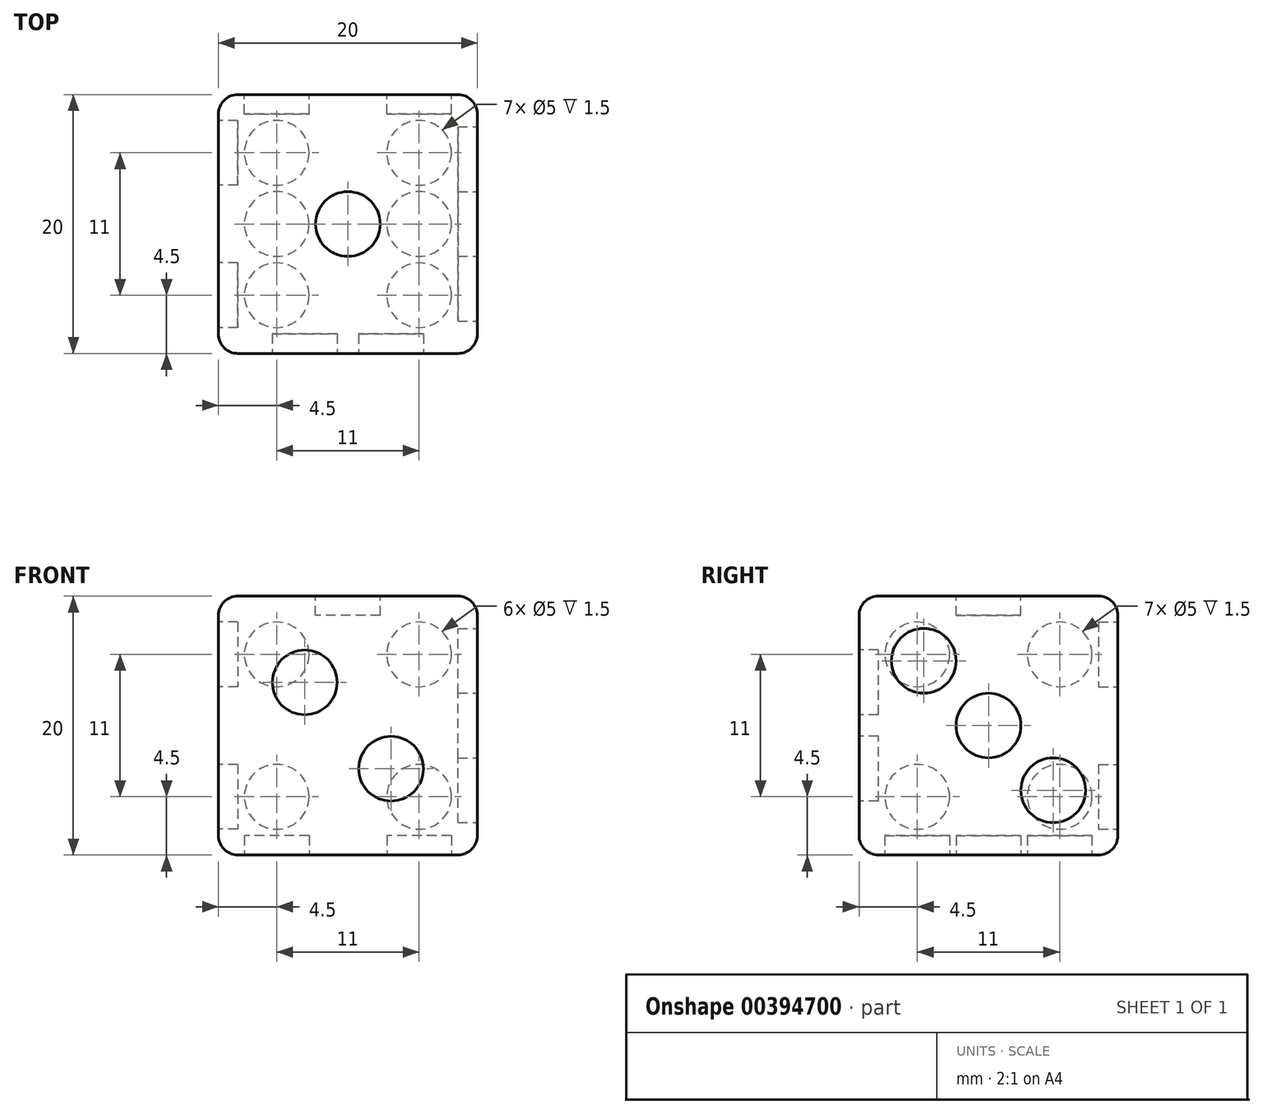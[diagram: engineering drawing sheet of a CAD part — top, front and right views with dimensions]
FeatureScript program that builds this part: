
annotation { "Feature Type Name" : "Feature", "Feature Type Description" : "" }
export const myFeature = defineFeature(function(context is Context, id is Id, definition is map)
    precondition{}
    {
        {
            assignVariable(context, id + "F0", {"name" : "Extrude", "anyValue" : -1.5});
        }
        {
            var Q0;
            Q0=qCreatedBy(makeId("Top.planeOp"),FACE);
            var sketch = newSketch(context, id + "F1", { "sketchPlane" : qUnion([Q0])});
            skLineSegment(sketch, "E0.bottom", {"start": v(10, 10) * mm, "end": v(-10, 10) * mm});
            skLineSegment(sketch, "E0.top", {"start": v(10, -10) * mm, "end": v(-10, -10) * mm});
            skLineSegment(sketch, "E0.left", {"start": v(10, 10) * mm, "end": v(10, -10) * mm});
            skLineSegment(sketch, "E0.right", {"start": v(-10, 10) * mm, "end": v(-10, -10) * mm});
            skPoint(sketch, "E0.middle", {"position": v(0, 0) * mm});
            skSolve(sketch);
        }
        {
            var Q0;
            Q0=makeQuery(id+"F1.imprint","IMPRINT",FACE,{"disambiguationData":[TD([[makeQuery(id+"F1.imprint","IMPRINT",EDGE,{"derivedFrom":sQuery(id+"F1.wireOp",EDGE,"E0.bottom")}),1.0]])]});
            extrude(context, id + "F2", {"entities" : qUnion([Q0]), "depth" : 20 * mm});
        }
        {
            var Q0;
            Q0=makeQuery(id+"F2.opExtrude","CAP_FACE",FACE,{"disambiguationData":[OSD([sQuery(id+"F1.wireOp",EDGE,"E0.bottom"),sQuery(id+"F1.wireOp",EDGE,"E0.top"),sQuery(id+"F1.wireOp",EDGE,"E0.left"),sQuery(id+"F1.wireOp",EDGE,"E0.right")])],"isStart":false});
            var sketch = newSketch(context, id + "F3", { "sketchPlane" : qUnion([Q0])});
            skCircle(sketch, "E1", {"center": v(0, 0) * mm, "radius": 2.5 * mm});
            skSolve(sketch);
        }
        {
            var Q0;
            Q0=makeQuery(id+"F1.imprint","IMPRINT",FACE,{"disambiguationData":[TD([[makeQuery(id+"F1.imprint","IMPRINT",EDGE,{"derivedFrom":sQuery(id+"F1.wireOp",EDGE,"E0.bottom")}),1.0]])]});
            var sketch = newSketch(context, id + "F4", { "sketchPlane" : qUnion([Q0])});
            skCircle(sketch, "E2", {"center": v(-5.5, -5.5) * mm, "radius": 2.5 * mm});
            skCircle(sketch, "E3", {"center": v(5.5, -5.5) * mm, "radius": 2.5 * mm});
            skCircle(sketch, "E4", {"center": v(5.5, 5.5) * mm, "radius": 2.5 * mm});
            skCircle(sketch, "E5", {"center": v(-5.5, 5.5) * mm, "radius": 2.5 * mm});
            skCircle(sketch, "E6", {"center": v(5.5, 0) * mm, "radius": 2.5 * mm});
            skCircle(sketch, "E7", {"center": v(-5.5, 0) * mm, "radius": 2.5 * mm});
            skLineSegment(sketch, "E8.0", {"start": v(10, -10) * mm, "end": v(-10, -10) * mm});
            skLineSegment(sketch, "E9.0", {"start": v(-10, 10) * mm, "end": v(-10, -10) * mm});
            skLineSegment(sketch, "E10.0", {"start": v(10, 10) * mm, "end": v(-10, 10) * mm});
            skLineSegment(sketch, "E11.0", {"start": v(10, 10) * mm, "end": v(10, -10) * mm});
            skLineSegment(sketch, "E12", {"start": v(-10, -10) * mm, "end": v(10, 10) * mm});
            skLineSegment(sketch, "E13", {"start": v(10, -10) * mm, "end": v(-10, 10) * mm});
            skLineSegment(sketch, "E14", {"start": v(-5.5, -5.5) * mm, "end": v(-5.5, 5.5) * mm});
            skLineSegment(sketch, "E15", {"start": v(5.5, -5.5) * mm, "end": v(5.5, 5.5) * mm});
            skSolve(sketch);
        }
        {
            var Q0;
            Q0=makeQuery(id+"F2.opExtrude","SWEPT_FACE",FACE,{"disambiguationData":[OSD([sQuery(id+"F1.wireOp",EDGE,"E0.bottom")])]});
            var sketch = newSketch(context, id + "F5", { "sketchPlane" : qUnion([Q0])});
            skLineSegment(sketch, "E16", {"start": v(-10, 0) * mm, "end": v(10, 20) * mm});
            skLineSegment(sketch, "E17", {"start": v(-10, 20) * mm, "end": v(10, 0) * mm});
            skCircle(sketch, "E18", {"center": v(0, 10) * mm, "radius": 2.5 * mm});
            skCircle(sketch, "E19", {"center": v(-5.5, 15.5) * mm, "radius": 2.5 * mm});
            skCircle(sketch, "E20", {"center": v(5.5, 15.5) * mm, "radius": 2.5 * mm});
            skCircle(sketch, "E21", {"center": v(5.5, 4.5) * mm, "radius": 2.5 * mm});
            skCircle(sketch, "E22", {"center": v(-5.5, 4.5) * mm, "radius": 2.5 * mm});
            skLineSegment(sketch, "E23.bottom", {"start": v(-5.5, 15.5) * mm, "end": v(5.5, 15.5) * mm});
            skLineSegment(sketch, "E23.top", {"start": v(-5.5, 4.5) * mm, "end": v(5.5, 4.5) * mm});
            skLineSegment(sketch, "E23.left", {"start": v(-5.5, 15.5) * mm, "end": v(-5.5, 4.5) * mm});
            skLineSegment(sketch, "E23.right", {"start": v(5.5, 15.5) * mm, "end": v(5.5, 4.5) * mm});
            skSolve(sketch);
        }
        {
            var Q0;
            Q0=makeQuery(id+"F2.opExtrude","SWEPT_FACE",FACE,{"disambiguationData":[OSD([sQuery(id+"F1.wireOp",EDGE,"E0.top")])]});
            var sketch = newSketch(context, id + "F6", { "sketchPlane" : qUnion([Q0])});
            skLineSegment(sketch, "E24", {"start": v(-10, 20) * mm, "end": v(-3.33, 13.33) * mm});
            skLineSegment(sketch, "E25", {"start": v(-3.33, 13.33) * mm, "end": v(3.33, 6.67) * mm});
            skLineSegment(sketch, "E26", {"start": v(3.33, 6.67) * mm, "end": v(10, 0) * mm});
            skCircle(sketch, "E27", {"center": v(-3.33, 13.33) * mm, "radius": 2.5 * mm});
            skCircle(sketch, "E28", {"center": v(3.33, 6.67) * mm, "radius": 2.5 * mm});
            skSolve(sketch);
        }
        {
            var Q0;
            Q0=makeQuery(id+"F2.opExtrude","SWEPT_FACE",FACE,{"disambiguationData":[OSD([sQuery(id+"F1.wireOp",EDGE,"E0.right")])]});
            var sketch = newSketch(context, id + "F7", { "sketchPlane" : qUnion([Q0])});
            skLineSegment(sketch, "E29", {"start": v(-10, 20) * mm, "end": v(10, 0) * mm});
            skLineSegment(sketch, "E30", {"start": v(10, 20) * mm, "end": v(-10, 0) * mm});
            skCircle(sketch, "E31", {"center": v(-5.5, 15.5) * mm, "radius": 2.5 * mm});
            skCircle(sketch, "E32", {"center": v(5.5, 15.5) * mm, "radius": 2.5 * mm});
            skCircle(sketch, "E33", {"center": v(-5.5, 4.5) * mm, "radius": 2.5 * mm});
            skCircle(sketch, "E34", {"center": v(5.5, 4.5) * mm, "radius": 2.5 * mm});
            skLineSegment(sketch, "E35.bottom", {"start": v(-5.5, 15.5) * mm, "end": v(5.5, 15.5) * mm});
            skLineSegment(sketch, "E35.top", {"start": v(-5.5, 4.5) * mm, "end": v(5.5, 4.5) * mm});
            skLineSegment(sketch, "E35.left", {"start": v(-5.5, 15.5) * mm, "end": v(-5.5, 4.5) * mm});
            skLineSegment(sketch, "E35.right", {"start": v(5.5, 15.5) * mm, "end": v(5.5, 4.5) * mm});
            skSolve(sketch);
        }
        {
            var Q0;
            Q0=makeQuery(id+"F2.opExtrude","SWEPT_FACE",FACE,{"disambiguationData":[OSD([sQuery(id+"F1.wireOp",EDGE,"E0.left")])]});
            var sketch = newSketch(context, id + "F8", { "sketchPlane" : qUnion([Q0])});
            skLineSegment(sketch, "E36", {"start": v(-10, 20) * mm, "end": v(-5, 15) * mm});
            skLineSegment(sketch, "E37", {"start": v(-5, 15) * mm, "end": v(0, 10) * mm});
            skLineSegment(sketch, "E38", {"start": v(0, 10) * mm, "end": v(5, 5) * mm});
            skLineSegment(sketch, "E39", {"start": v(5, 5) * mm, "end": v(10, 0) * mm});
            skCircle(sketch, "E40", {"center": v(-5, 15) * mm, "radius": 2.5 * mm});
            skCircle(sketch, "E41", {"center": v(0, 10) * mm, "radius": 2.5 * mm});
            skCircle(sketch, "E42", {"center": v(5, 5) * mm, "radius": 2.5 * mm});
            skSolve(sketch);
        }
        {
            var Q0;
            Q0=makeQuery(id+"F3.imprint","IMPRINT",FACE,{"disambiguationData":[TD([[makeQuery(id+"F3.imprint","IMPRINT",EDGE,{"derivedFrom":sQuery(id+"F3.wireOp",EDGE,"E1")}),1.0]])]});
            extrude(context, id + "F9", {"entities" : qUnion([Q0]), "operationType" : NewBodyOperationType.REMOVE, "depth" : (getVariable(context, 'Extrude')) * mm});
        }
        {
            var Q0;
            {var subQ0=sQuery(id+"F6.wireOp",EDGE,"E25");var subQ1=sQuery(id+"F6.wireOp",EDGE,"E24");var subQ2=makeQuery(id+"F6.imprint","INTERSECT",VERTEX,{"derivedFrom":[subQ1,subQ0]});Q0=makeQuery(id+"F6.imprint","IMPRINT",FACE,{"disambiguationData":[TD([[makeQuery(id+"F6.imprint","IMPRINT",EDGE,{"disambiguationData":[TD([[subQ2,1.0]])],"derivedFrom":subQ1}),1.0]])]});}
            var Q1;
            {var subQ0=sQuery(id+"F6.wireOp",EDGE,"E25");var subQ1=sQuery(id+"F6.wireOp",EDGE,"E24");var subQ2=makeQuery(id+"F6.imprint","INTERSECT",VERTEX,{"derivedFrom":[subQ1,subQ0]});Q1=makeQuery(id+"F6.imprint","IMPRINT",FACE,{"disambiguationData":[TD([[makeQuery(id+"F6.imprint","IMPRINT",EDGE,{"disambiguationData":[TD([[subQ2,1.0]])],"derivedFrom":subQ1}),-1.0]])]});}
            var Q2;
            {var subQ0=sQuery(id+"F6.wireOp",EDGE,"E26");var subQ1=sQuery(id+"F6.wireOp",EDGE,"E25");var subQ2=makeQuery(id+"F6.imprint","INTERSECT",VERTEX,{"derivedFrom":[subQ1,subQ0]});Q2=makeQuery(id+"F6.imprint","IMPRINT",FACE,{"disambiguationData":[TD([[makeQuery(id+"F6.imprint","IMPRINT",EDGE,{"disambiguationData":[TD([[subQ2,1.0]])],"derivedFrom":subQ1}),1.0]])]});}
            var Q3;
            {var subQ0=sQuery(id+"F6.wireOp",EDGE,"E26");var subQ1=sQuery(id+"F6.wireOp",EDGE,"E25");var subQ2=makeQuery(id+"F6.imprint","INTERSECT",VERTEX,{"derivedFrom":[subQ1,subQ0]});Q3=makeQuery(id+"F6.imprint","IMPRINT",FACE,{"disambiguationData":[TD([[makeQuery(id+"F6.imprint","IMPRINT",EDGE,{"disambiguationData":[TD([[subQ2,1.0]])],"derivedFrom":subQ1}),-1.0]])]});}
            extrude(context, id + "F10", {"entities" : qUnion([Q0, Q1, Q2, Q3]), "operationType" : NewBodyOperationType.REMOVE, "depth" : (getVariable(context, 'Extrude')) * mm});
        }
        {
            var Q0;
            {var subQ0=sQuery(id+"F8.wireOp",EDGE,"E37");var subQ1=sQuery(id+"F8.wireOp",EDGE,"E36");var subQ2=makeQuery(id+"F8.imprint","INTERSECT",VERTEX,{"derivedFrom":[subQ1,subQ0]});Q0=makeQuery(id+"F8.imprint","IMPRINT",FACE,{"disambiguationData":[TD([[makeQuery(id+"F8.imprint","IMPRINT",EDGE,{"disambiguationData":[TD([[subQ2,1.0]])],"derivedFrom":subQ1}),-1.0]])]});}
            var Q1;
            {var subQ0=sQuery(id+"F8.wireOp",EDGE,"E37");var subQ1=sQuery(id+"F8.wireOp",EDGE,"E36");var subQ2=makeQuery(id+"F8.imprint","INTERSECT",VERTEX,{"derivedFrom":[subQ1,subQ0]});Q1=makeQuery(id+"F8.imprint","IMPRINT",FACE,{"disambiguationData":[TD([[makeQuery(id+"F8.imprint","IMPRINT",EDGE,{"disambiguationData":[TD([[subQ2,1.0]])],"derivedFrom":subQ1}),1.0]])]});}
            var Q2;
            {var subQ0=sQuery(id+"F8.wireOp",EDGE,"E38");var subQ1=sQuery(id+"F8.wireOp",EDGE,"E37");var subQ2=makeQuery(id+"F8.imprint","INTERSECT",VERTEX,{"derivedFrom":[subQ1,subQ0]});Q2=makeQuery(id+"F8.imprint","IMPRINT",FACE,{"disambiguationData":[TD([[makeQuery(id+"F8.imprint","IMPRINT",EDGE,{"disambiguationData":[TD([[subQ2,1.0]])],"derivedFrom":subQ1}),-1.0]])]});}
            var Q3;
            {var subQ0=sQuery(id+"F8.wireOp",EDGE,"E38");var subQ1=sQuery(id+"F8.wireOp",EDGE,"E37");var subQ2=makeQuery(id+"F8.imprint","INTERSECT",VERTEX,{"derivedFrom":[subQ1,subQ0]});Q3=makeQuery(id+"F8.imprint","IMPRINT",FACE,{"disambiguationData":[TD([[makeQuery(id+"F8.imprint","IMPRINT",EDGE,{"disambiguationData":[TD([[subQ2,1.0]])],"derivedFrom":subQ1}),1.0]])]});}
            var Q4;
            {var subQ0=sQuery(id+"F8.wireOp",EDGE,"E39");var subQ1=sQuery(id+"F8.wireOp",EDGE,"E38");var subQ2=makeQuery(id+"F8.imprint","INTERSECT",VERTEX,{"derivedFrom":[subQ1,subQ0]});Q4=makeQuery(id+"F8.imprint","IMPRINT",FACE,{"disambiguationData":[TD([[makeQuery(id+"F8.imprint","IMPRINT",EDGE,{"disambiguationData":[TD([[subQ2,1.0]])],"derivedFrom":subQ1}),-1.0]])]});}
            var Q5;
            {var subQ0=sQuery(id+"F8.wireOp",EDGE,"E39");var subQ1=sQuery(id+"F8.wireOp",EDGE,"E38");var subQ2=makeQuery(id+"F8.imprint","INTERSECT",VERTEX,{"derivedFrom":[subQ1,subQ0]});Q5=makeQuery(id+"F8.imprint","IMPRINT",FACE,{"disambiguationData":[TD([[makeQuery(id+"F8.imprint","IMPRINT",EDGE,{"disambiguationData":[TD([[subQ2,1.0]])],"derivedFrom":subQ1}),1.0]])]});}
            extrude(context, id + "F11", {"entities" : qUnion([Q0, Q1, Q2, Q3, Q4, Q5]), "operationType" : NewBodyOperationType.REMOVE, "depth" : (getVariable(context, 'Extrude')) * mm});
        }
        {
            var Q0;
            {var subQ1=sQuery(id+"F7.wireOp",EDGE,"E29");var subQ3=sQuery(id+"F7.wireOp",EDGE,"E31");var subQ4=makeQuery(id+"F7.imprint","INTERSECT",VERTEX,{"disambiguationData":[OD(0.0)],"derivedFrom":[subQ1,subQ3]});Q0=makeQuery(id+"F7.imprint","IMPRINT",FACE,{"disambiguationData":[TD([[makeQuery(id+"F7.imprint","IMPRINT",EDGE,{"disambiguationData":[TD([[subQ4,1.0]])],"derivedFrom":subQ3}),1.0]])]});}
            var Q1;
            {var subQ1=sQuery(id+"F7.wireOp",EDGE,"E29");var subQ3=sQuery(id+"F7.wireOp",EDGE,"E31");var subQ4=makeQuery(id+"F7.imprint","INTERSECT",VERTEX,{"disambiguationData":[OD(0.0)],"derivedFrom":[subQ1,subQ3]});Q1=makeQuery(id+"F7.imprint","IMPRINT",FACE,{"disambiguationData":[TD([[makeQuery(id+"F7.imprint","IMPRINT",EDGE,{"disambiguationData":[TD([[subQ4,-1.0]])],"derivedFrom":subQ3}),1.0]])]});}
            var Q2;
            {var subQ1=sQuery(id+"F7.wireOp",EDGE,"E29");var subQ3=sQuery(id+"F7.wireOp",EDGE,"E31");var subQ4=makeQuery(id+"F7.imprint","INTERSECT",VERTEX,{"disambiguationData":[OD(1.0)],"derivedFrom":[subQ1,subQ3]});Q2=makeQuery(id+"F7.imprint","IMPRINT",FACE,{"disambiguationData":[TD([[makeQuery(id+"F7.imprint","IMPRINT",EDGE,{"disambiguationData":[TD([[subQ4,1.0]])],"derivedFrom":subQ3}),1.0]])]});}
            var Q3;
            {var subQ1=sQuery(id+"F7.wireOp",EDGE,"E29");var subQ3=sQuery(id+"F7.wireOp",EDGE,"E31");var subQ4=makeQuery(id+"F7.imprint","INTERSECT",VERTEX,{"disambiguationData":[OD(1.0)],"derivedFrom":[subQ1,subQ3]});Q3=makeQuery(id+"F7.imprint","IMPRINT",FACE,{"disambiguationData":[TD([[makeQuery(id+"F7.imprint","IMPRINT",EDGE,{"disambiguationData":[TD([[subQ4,-1.0]])],"derivedFrom":subQ3}),1.0]])]});}
            var Q4;
            {var subQ1=sQuery(id+"F7.wireOp",EDGE,"E30");var subQ3=sQuery(id+"F7.wireOp",EDGE,"E32");var subQ4=makeQuery(id+"F7.imprint","INTERSECT",VERTEX,{"disambiguationData":[OD(0.0)],"derivedFrom":[subQ1,subQ3]});Q4=makeQuery(id+"F7.imprint","IMPRINT",FACE,{"disambiguationData":[TD([[makeQuery(id+"F7.imprint","IMPRINT",EDGE,{"disambiguationData":[TD([[subQ4,-1.0]])],"derivedFrom":subQ3}),1.0]])]});}
            var Q5;
            {var subQ1=sQuery(id+"F7.wireOp",EDGE,"E30");var subQ3=sQuery(id+"F7.wireOp",EDGE,"E32");var subQ4=makeQuery(id+"F7.imprint","INTERSECT",VERTEX,{"disambiguationData":[OD(0.0)],"derivedFrom":[subQ1,subQ3]});Q5=makeQuery(id+"F7.imprint","IMPRINT",FACE,{"disambiguationData":[TD([[makeQuery(id+"F7.imprint","IMPRINT",EDGE,{"disambiguationData":[TD([[subQ4,1.0]])],"derivedFrom":subQ3}),1.0]])]});}
            var Q6;
            {var subQ1=sQuery(id+"F7.wireOp",EDGE,"E30");var subQ3=sQuery(id+"F7.wireOp",EDGE,"E32");var subQ4=makeQuery(id+"F7.imprint","INTERSECT",VERTEX,{"disambiguationData":[OD(1.0)],"derivedFrom":[subQ1,subQ3]});Q6=makeQuery(id+"F7.imprint","IMPRINT",FACE,{"disambiguationData":[TD([[makeQuery(id+"F7.imprint","IMPRINT",EDGE,{"disambiguationData":[TD([[subQ4,-1.0]])],"derivedFrom":subQ3}),1.0]])]});}
            var Q7;
            {var subQ1=sQuery(id+"F7.wireOp",EDGE,"E30");var subQ3=sQuery(id+"F7.wireOp",EDGE,"E32");var subQ4=makeQuery(id+"F7.imprint","INTERSECT",VERTEX,{"disambiguationData":[OD(1.0)],"derivedFrom":[subQ1,subQ3]});Q7=makeQuery(id+"F7.imprint","IMPRINT",FACE,{"disambiguationData":[TD([[makeQuery(id+"F7.imprint","IMPRINT",EDGE,{"disambiguationData":[TD([[subQ4,1.0]])],"derivedFrom":subQ3}),1.0]])]});}
            var Q8;
            {var subQ1=sQuery(id+"F7.wireOp",EDGE,"E29");var subQ3=sQuery(id+"F7.wireOp",EDGE,"E34");var subQ4=makeQuery(id+"F7.imprint","INTERSECT",VERTEX,{"disambiguationData":[OD(1.0)],"derivedFrom":[subQ1,subQ3]});Q8=makeQuery(id+"F7.imprint","IMPRINT",FACE,{"disambiguationData":[TD([[makeQuery(id+"F7.imprint","IMPRINT",EDGE,{"disambiguationData":[TD([[subQ4,-1.0]])],"derivedFrom":subQ3}),1.0]])]});}
            var Q9;
            {var subQ1=sQuery(id+"F7.wireOp",EDGE,"E29");var subQ3=sQuery(id+"F7.wireOp",EDGE,"E34");var subQ4=makeQuery(id+"F7.imprint","INTERSECT",VERTEX,{"disambiguationData":[OD(1.0)],"derivedFrom":[subQ1,subQ3]});Q9=makeQuery(id+"F7.imprint","IMPRINT",FACE,{"disambiguationData":[TD([[makeQuery(id+"F7.imprint","IMPRINT",EDGE,{"disambiguationData":[TD([[subQ4,1.0]])],"derivedFrom":subQ3}),1.0]])]});}
            var Q10;
            {var subQ1=sQuery(id+"F7.wireOp",EDGE,"E29");var subQ3=sQuery(id+"F7.wireOp",EDGE,"E34");var subQ4=makeQuery(id+"F7.imprint","INTERSECT",VERTEX,{"disambiguationData":[OD(0.0)],"derivedFrom":[subQ1,subQ3]});Q10=makeQuery(id+"F7.imprint","IMPRINT",FACE,{"disambiguationData":[TD([[makeQuery(id+"F7.imprint","IMPRINT",EDGE,{"disambiguationData":[TD([[subQ4,1.0]])],"derivedFrom":subQ3}),1.0]])]});}
            var Q11;
            {var subQ1=sQuery(id+"F7.wireOp",EDGE,"E29");var subQ3=sQuery(id+"F7.wireOp",EDGE,"E34");var subQ4=makeQuery(id+"F7.imprint","INTERSECT",VERTEX,{"disambiguationData":[OD(0.0)],"derivedFrom":[subQ1,subQ3]});Q11=makeQuery(id+"F7.imprint","IMPRINT",FACE,{"disambiguationData":[TD([[makeQuery(id+"F7.imprint","IMPRINT",EDGE,{"disambiguationData":[TD([[subQ4,-1.0]])],"derivedFrom":subQ3}),1.0]])]});}
            var Q12;
            {var subQ1=sQuery(id+"F7.wireOp",EDGE,"E30");var subQ3=sQuery(id+"F7.wireOp",EDGE,"E33");var subQ4=makeQuery(id+"F7.imprint","INTERSECT",VERTEX,{"disambiguationData":[OD(1.0)],"derivedFrom":[subQ1,subQ3]});Q12=makeQuery(id+"F7.imprint","IMPRINT",FACE,{"disambiguationData":[TD([[makeQuery(id+"F7.imprint","IMPRINT",EDGE,{"disambiguationData":[TD([[subQ4,-1.0]])],"derivedFrom":subQ3}),1.0]])]});}
            var Q13;
            {var subQ1=sQuery(id+"F7.wireOp",EDGE,"E30");var subQ3=sQuery(id+"F7.wireOp",EDGE,"E33");var subQ4=makeQuery(id+"F7.imprint","INTERSECT",VERTEX,{"disambiguationData":[OD(0.0)],"derivedFrom":[subQ1,subQ3]});Q13=makeQuery(id+"F7.imprint","IMPRINT",FACE,{"disambiguationData":[TD([[makeQuery(id+"F7.imprint","IMPRINT",EDGE,{"disambiguationData":[TD([[subQ4,1.0]])],"derivedFrom":subQ3}),1.0]])]});}
            var Q14;
            {var subQ1=sQuery(id+"F7.wireOp",EDGE,"E30");var subQ3=sQuery(id+"F7.wireOp",EDGE,"E33");var subQ4=makeQuery(id+"F7.imprint","INTERSECT",VERTEX,{"disambiguationData":[OD(0.0)],"derivedFrom":[subQ1,subQ3]});Q14=makeQuery(id+"F7.imprint","IMPRINT",FACE,{"disambiguationData":[TD([[makeQuery(id+"F7.imprint","IMPRINT",EDGE,{"disambiguationData":[TD([[subQ4,-1.0]])],"derivedFrom":subQ3}),1.0]])]});}
            var Q15;
            {var subQ1=sQuery(id+"F7.wireOp",EDGE,"E30");var subQ3=sQuery(id+"F7.wireOp",EDGE,"E33");var subQ4=makeQuery(id+"F7.imprint","INTERSECT",VERTEX,{"disambiguationData":[OD(1.0)],"derivedFrom":[subQ1,subQ3]});Q15=makeQuery(id+"F7.imprint","IMPRINT",FACE,{"disambiguationData":[TD([[makeQuery(id+"F7.imprint","IMPRINT",EDGE,{"disambiguationData":[TD([[subQ4,1.0]])],"derivedFrom":subQ3}),1.0]])]});}
            extrude(context, id + "F12", {"entities" : qUnion([Q0, Q1, Q2, Q3, Q4, Q5, Q6, Q7, Q8, Q9, Q10, Q11, Q12, Q13, Q14, Q15]), "operationType" : NewBodyOperationType.REMOVE, "depth" : (getVariable(context, 'Extrude')) * mm});
        }
        {
            var Q0;
            {var subQ1=sQuery(id+"F5.wireOp",EDGE,"E16");var subQ3=sQuery(id+"F5.wireOp",EDGE,"E22");var subQ4=makeQuery(id+"F5.imprint","INTERSECT",VERTEX,{"disambiguationData":[OD(0.0)],"derivedFrom":[subQ1,subQ3]});Q0=makeQuery(id+"F5.imprint","IMPRINT",FACE,{"disambiguationData":[TD([[makeQuery(id+"F5.imprint","IMPRINT",EDGE,{"disambiguationData":[TD([[subQ4,1.0]])],"derivedFrom":subQ3}),1.0]])]});}
            var Q1;
            {var subQ1=sQuery(id+"F5.wireOp",EDGE,"E16");var subQ3=sQuery(id+"F5.wireOp",EDGE,"E22");var subQ4=makeQuery(id+"F5.imprint","INTERSECT",VERTEX,{"disambiguationData":[OD(1.0)],"derivedFrom":[subQ1,subQ3]});Q1=makeQuery(id+"F5.imprint","IMPRINT",FACE,{"disambiguationData":[TD([[makeQuery(id+"F5.imprint","IMPRINT",EDGE,{"disambiguationData":[TD([[subQ4,-1.0]])],"derivedFrom":subQ3}),1.0]])]});}
            var Q2;
            {var subQ1=sQuery(id+"F5.wireOp",EDGE,"E16");var subQ3=sQuery(id+"F5.wireOp",EDGE,"E22");var subQ4=makeQuery(id+"F5.imprint","INTERSECT",VERTEX,{"disambiguationData":[OD(0.0)],"derivedFrom":[subQ1,subQ3]});Q2=makeQuery(id+"F5.imprint","IMPRINT",FACE,{"disambiguationData":[TD([[makeQuery(id+"F5.imprint","IMPRINT",EDGE,{"disambiguationData":[TD([[subQ4,-1.0]])],"derivedFrom":subQ3}),1.0]])]});}
            var Q3;
            {var subQ1=sQuery(id+"F5.wireOp",EDGE,"E16");var subQ3=sQuery(id+"F5.wireOp",EDGE,"E22");var subQ4=makeQuery(id+"F5.imprint","INTERSECT",VERTEX,{"disambiguationData":[OD(1.0)],"derivedFrom":[subQ1,subQ3]});Q3=makeQuery(id+"F5.imprint","IMPRINT",FACE,{"disambiguationData":[TD([[makeQuery(id+"F5.imprint","IMPRINT",EDGE,{"disambiguationData":[TD([[subQ4,1.0]])],"derivedFrom":subQ3}),1.0]])]});}
            var Q4;
            {var subQ1=sQuery(id+"F5.wireOp",EDGE,"E17");var subQ3=sQuery(id+"F5.wireOp",EDGE,"E19");var subQ4=makeQuery(id+"F5.imprint","INTERSECT",VERTEX,{"disambiguationData":[OD(0.0)],"derivedFrom":[subQ1,subQ3]});Q4=makeQuery(id+"F5.imprint","IMPRINT",FACE,{"disambiguationData":[TD([[makeQuery(id+"F5.imprint","IMPRINT",EDGE,{"disambiguationData":[TD([[subQ4,-1.0]])],"derivedFrom":subQ3}),1.0]])]});}
            var Q5;
            {var subQ1=sQuery(id+"F5.wireOp",EDGE,"E17");var subQ3=sQuery(id+"F5.wireOp",EDGE,"E19");var subQ4=makeQuery(id+"F5.imprint","INTERSECT",VERTEX,{"disambiguationData":[OD(0.0)],"derivedFrom":[subQ1,subQ3]});Q5=makeQuery(id+"F5.imprint","IMPRINT",FACE,{"disambiguationData":[TD([[makeQuery(id+"F5.imprint","IMPRINT",EDGE,{"disambiguationData":[TD([[subQ4,1.0]])],"derivedFrom":subQ3}),1.0]])]});}
            var Q6;
            {var subQ1=sQuery(id+"F5.wireOp",EDGE,"E17");var subQ3=sQuery(id+"F5.wireOp",EDGE,"E19");var subQ4=makeQuery(id+"F5.imprint","INTERSECT",VERTEX,{"disambiguationData":[OD(1.0)],"derivedFrom":[subQ1,subQ3]});Q6=makeQuery(id+"F5.imprint","IMPRINT",FACE,{"disambiguationData":[TD([[makeQuery(id+"F5.imprint","IMPRINT",EDGE,{"disambiguationData":[TD([[subQ4,-1.0]])],"derivedFrom":subQ3}),1.0]])]});}
            var Q7;
            {var subQ1=sQuery(id+"F5.wireOp",EDGE,"E17");var subQ3=sQuery(id+"F5.wireOp",EDGE,"E19");var subQ4=makeQuery(id+"F5.imprint","INTERSECT",VERTEX,{"disambiguationData":[OD(1.0)],"derivedFrom":[subQ1,subQ3]});Q7=makeQuery(id+"F5.imprint","IMPRINT",FACE,{"disambiguationData":[TD([[makeQuery(id+"F5.imprint","IMPRINT",EDGE,{"disambiguationData":[TD([[subQ4,1.0]])],"derivedFrom":subQ3}),1.0]])]});}
            var Q8;
            {var subQ1=sQuery(id+"F5.wireOp",EDGE,"E16");var subQ3=sQuery(id+"F5.wireOp",EDGE,"E20");var subQ4=makeQuery(id+"F5.imprint","INTERSECT",VERTEX,{"disambiguationData":[OD(1.0)],"derivedFrom":[subQ1,subQ3]});Q8=makeQuery(id+"F5.imprint","IMPRINT",FACE,{"disambiguationData":[TD([[makeQuery(id+"F5.imprint","IMPRINT",EDGE,{"disambiguationData":[TD([[subQ4,1.0]])],"derivedFrom":subQ3}),1.0]])]});}
            var Q9;
            {var subQ1=sQuery(id+"F5.wireOp",EDGE,"E16");var subQ3=sQuery(id+"F5.wireOp",EDGE,"E20");var subQ4=makeQuery(id+"F5.imprint","INTERSECT",VERTEX,{"disambiguationData":[OD(0.0)],"derivedFrom":[subQ1,subQ3]});Q9=makeQuery(id+"F5.imprint","IMPRINT",FACE,{"disambiguationData":[TD([[makeQuery(id+"F5.imprint","IMPRINT",EDGE,{"disambiguationData":[TD([[subQ4,-1.0]])],"derivedFrom":subQ3}),1.0]])]});}
            var Q10;
            {var subQ1=sQuery(id+"F5.wireOp",EDGE,"E16");var subQ3=sQuery(id+"F5.wireOp",EDGE,"E20");var subQ4=makeQuery(id+"F5.imprint","INTERSECT",VERTEX,{"disambiguationData":[OD(0.0)],"derivedFrom":[subQ1,subQ3]});Q10=makeQuery(id+"F5.imprint","IMPRINT",FACE,{"disambiguationData":[TD([[makeQuery(id+"F5.imprint","IMPRINT",EDGE,{"disambiguationData":[TD([[subQ4,1.0]])],"derivedFrom":subQ3}),1.0]])]});}
            var Q11;
            {var subQ1=sQuery(id+"F5.wireOp",EDGE,"E16");var subQ3=sQuery(id+"F5.wireOp",EDGE,"E20");var subQ4=makeQuery(id+"F5.imprint","INTERSECT",VERTEX,{"disambiguationData":[OD(1.0)],"derivedFrom":[subQ1,subQ3]});Q11=makeQuery(id+"F5.imprint","IMPRINT",FACE,{"disambiguationData":[TD([[makeQuery(id+"F5.imprint","IMPRINT",EDGE,{"disambiguationData":[TD([[subQ4,-1.0]])],"derivedFrom":subQ3}),1.0]])]});}
            var Q12;
            {var subQ1=sQuery(id+"F5.wireOp",EDGE,"E17");var subQ3=sQuery(id+"F5.wireOp",EDGE,"E21");var subQ4=makeQuery(id+"F5.imprint","INTERSECT",VERTEX,{"disambiguationData":[OD(1.0)],"derivedFrom":[subQ1,subQ3]});Q12=makeQuery(id+"F5.imprint","IMPRINT",FACE,{"disambiguationData":[TD([[makeQuery(id+"F5.imprint","IMPRINT",EDGE,{"disambiguationData":[TD([[subQ4,-1.0]])],"derivedFrom":subQ3}),1.0]])]});}
            var Q13;
            {var subQ1=sQuery(id+"F5.wireOp",EDGE,"E17");var subQ3=sQuery(id+"F5.wireOp",EDGE,"E21");var subQ4=makeQuery(id+"F5.imprint","INTERSECT",VERTEX,{"disambiguationData":[OD(0.0)],"derivedFrom":[subQ1,subQ3]});Q13=makeQuery(id+"F5.imprint","IMPRINT",FACE,{"disambiguationData":[TD([[makeQuery(id+"F5.imprint","IMPRINT",EDGE,{"disambiguationData":[TD([[subQ4,-1.0]])],"derivedFrom":subQ3}),1.0]])]});}
            var Q14;
            {var subQ1=sQuery(id+"F5.wireOp",EDGE,"E17");var subQ3=sQuery(id+"F5.wireOp",EDGE,"E21");var subQ4=makeQuery(id+"F5.imprint","INTERSECT",VERTEX,{"disambiguationData":[OD(0.0)],"derivedFrom":[subQ1,subQ3]});Q14=makeQuery(id+"F5.imprint","IMPRINT",FACE,{"disambiguationData":[TD([[makeQuery(id+"F5.imprint","IMPRINT",EDGE,{"disambiguationData":[TD([[subQ4,1.0]])],"derivedFrom":subQ3}),1.0]])]});}
            var Q15;
            {var subQ1=sQuery(id+"F5.wireOp",EDGE,"E17");var subQ3=sQuery(id+"F5.wireOp",EDGE,"E21");var subQ4=makeQuery(id+"F5.imprint","INTERSECT",VERTEX,{"disambiguationData":[OD(1.0)],"derivedFrom":[subQ1,subQ3]});Q15=makeQuery(id+"F5.imprint","IMPRINT",FACE,{"disambiguationData":[TD([[makeQuery(id+"F5.imprint","IMPRINT",EDGE,{"disambiguationData":[TD([[subQ4,1.0]])],"derivedFrom":subQ3}),1.0]])]});}
            extrude(context, id + "F13", {"entities" : qUnion([Q0, Q1, Q2, Q3, Q4, Q5, Q6, Q7, Q8, Q9, Q10, Q11, Q12, Q13, Q14, Q15]), "operationType" : NewBodyOperationType.REMOVE, "depth" : (getVariable(context, 'Extrude')) * mm});
        }
        {
            var Q0;
            {var subQ0=sQuery(id+"F4.wireOp",EDGE,"E15");var subQ1=sQuery(id+"F4.wireOp",EDGE,"E3");var subQ2=makeQuery(id+"F4.imprint","INTERSECT",VERTEX,{"derivedFrom":[subQ1,subQ0]});Q0=makeQuery(id+"F4.imprint","IMPRINT",FACE,{"disambiguationData":[TD([[makeQuery(id+"F4.imprint","IMPRINT",EDGE,{"disambiguationData":[TD([[subQ2,1.0]])],"derivedFrom":subQ1}),1.0]])]});}
            var Q1;
            {var subQ0=sQuery(id+"F4.wireOp",EDGE,"E13");var subQ1=sQuery(id+"F4.wireOp",EDGE,"E3");var subQ2=makeQuery(id+"F4.imprint","INTERSECT",VERTEX,{"disambiguationData":[OD(0.0)],"derivedFrom":[subQ1,subQ0]});Q1=makeQuery(id+"F4.imprint","IMPRINT",FACE,{"disambiguationData":[TD([[makeQuery(id+"F4.imprint","IMPRINT",EDGE,{"disambiguationData":[TD([[subQ2,1.0]])],"derivedFrom":subQ1}),1.0]])]});}
            var Q2;
            {var subQ0=sQuery(id+"F4.wireOp",EDGE,"E13");var subQ1=sQuery(id+"F4.wireOp",EDGE,"E3");var subQ2=makeQuery(id+"F4.imprint","INTERSECT",VERTEX,{"disambiguationData":[OD(0.0)],"derivedFrom":[subQ1,subQ0]});Q2=makeQuery(id+"F4.imprint","IMPRINT",FACE,{"disambiguationData":[TD([[makeQuery(id+"F4.imprint","IMPRINT",EDGE,{"disambiguationData":[TD([[subQ2,-1.0]])],"derivedFrom":subQ1}),1.0]])]});}
            var Q3;
            {var subQ0=sQuery(id+"F4.wireOp",EDGE,"E15");var subQ1=sQuery(id+"F4.wireOp",EDGE,"E6");var subQ2=makeQuery(id+"F4.imprint","INTERSECT",VERTEX,{"disambiguationData":[OD(0.0)],"derivedFrom":[subQ1,subQ0]});Q3=makeQuery(id+"F4.imprint","IMPRINT",FACE,{"disambiguationData":[TD([[makeQuery(id+"F4.imprint","IMPRINT",EDGE,{"disambiguationData":[TD([[subQ2,1.0]])],"derivedFrom":subQ1}),1.0]])]});}
            var Q4;
            {var subQ0=sQuery(id+"F4.wireOp",EDGE,"E15");var subQ1=sQuery(id+"F4.wireOp",EDGE,"E6");var subQ2=makeQuery(id+"F4.imprint","INTERSECT",VERTEX,{"disambiguationData":[OD(0.0)],"derivedFrom":[subQ1,subQ0]});Q4=makeQuery(id+"F4.imprint","IMPRINT",FACE,{"disambiguationData":[TD([[makeQuery(id+"F4.imprint","IMPRINT",EDGE,{"disambiguationData":[TD([[subQ2,-1.0]])],"derivedFrom":subQ1}),1.0]])]});}
            var Q5;
            {var subQ0=sQuery(id+"F4.wireOp",EDGE,"E12");var subQ1=sQuery(id+"F4.wireOp",EDGE,"E4");var subQ2=makeQuery(id+"F4.imprint","INTERSECT",VERTEX,{"disambiguationData":[OD(1.0)],"derivedFrom":[subQ1,subQ0]});Q5=makeQuery(id+"F4.imprint","IMPRINT",FACE,{"disambiguationData":[TD([[makeQuery(id+"F4.imprint","IMPRINT",EDGE,{"disambiguationData":[TD([[subQ2,1.0]])],"derivedFrom":subQ1}),1.0]])]});}
            var Q6;
            {var subQ0=sQuery(id+"F4.wireOp",EDGE,"E12");var subQ1=sQuery(id+"F4.wireOp",EDGE,"E4");var subQ2=makeQuery(id+"F4.imprint","INTERSECT",VERTEX,{"disambiguationData":[OD(0.0)],"derivedFrom":[subQ1,subQ0]});Q6=makeQuery(id+"F4.imprint","IMPRINT",FACE,{"disambiguationData":[TD([[makeQuery(id+"F4.imprint","IMPRINT",EDGE,{"disambiguationData":[TD([[subQ2,-1.0]])],"derivedFrom":subQ1}),1.0]])]});}
            var Q7;
            {var subQ0=sQuery(id+"F4.wireOp",EDGE,"E12");var subQ1=sQuery(id+"F4.wireOp",EDGE,"E4");var subQ2=makeQuery(id+"F4.imprint","INTERSECT",VERTEX,{"disambiguationData":[OD(0.0)],"derivedFrom":[subQ1,subQ0]});Q7=makeQuery(id+"F4.imprint","IMPRINT",FACE,{"disambiguationData":[TD([[makeQuery(id+"F4.imprint","IMPRINT",EDGE,{"disambiguationData":[TD([[subQ2,1.0]])],"derivedFrom":subQ1}),1.0]])]});}
            var Q8;
            {var subQ0=sQuery(id+"F4.wireOp",EDGE,"E14");var subQ1=sQuery(id+"F4.wireOp",EDGE,"E5");var subQ2=makeQuery(id+"F4.imprint","INTERSECT",VERTEX,{"derivedFrom":[subQ1,subQ0]});Q8=makeQuery(id+"F4.imprint","IMPRINT",FACE,{"disambiguationData":[TD([[makeQuery(id+"F4.imprint","IMPRINT",EDGE,{"disambiguationData":[TD([[subQ2,-1.0]])],"derivedFrom":subQ1}),1.0]])]});}
            var Q9;
            {var subQ0=sQuery(id+"F4.wireOp",EDGE,"E13");var subQ1=sQuery(id+"F4.wireOp",EDGE,"E5");var subQ2=makeQuery(id+"F4.imprint","INTERSECT",VERTEX,{"disambiguationData":[OD(0.0)],"derivedFrom":[subQ1,subQ0]});Q9=makeQuery(id+"F4.imprint","IMPRINT",FACE,{"disambiguationData":[TD([[makeQuery(id+"F4.imprint","IMPRINT",EDGE,{"disambiguationData":[TD([[subQ2,1.0]])],"derivedFrom":subQ1}),1.0]])]});}
            var Q10;
            {var subQ0=sQuery(id+"F4.wireOp",EDGE,"E14");var subQ1=sQuery(id+"F4.wireOp",EDGE,"E5");var subQ2=makeQuery(id+"F4.imprint","INTERSECT",VERTEX,{"derivedFrom":[subQ1,subQ0]});Q10=makeQuery(id+"F4.imprint","IMPRINT",FACE,{"disambiguationData":[TD([[makeQuery(id+"F4.imprint","IMPRINT",EDGE,{"disambiguationData":[TD([[subQ2,1.0]])],"derivedFrom":subQ1}),1.0]])]});}
            var Q11;
            {var subQ0=sQuery(id+"F4.wireOp",EDGE,"E14");var subQ1=sQuery(id+"F4.wireOp",EDGE,"E7");var subQ2=makeQuery(id+"F4.imprint","INTERSECT",VERTEX,{"disambiguationData":[OD(0.0)],"derivedFrom":[subQ1,subQ0]});Q11=makeQuery(id+"F4.imprint","IMPRINT",FACE,{"disambiguationData":[TD([[makeQuery(id+"F4.imprint","IMPRINT",EDGE,{"disambiguationData":[TD([[subQ2,1.0]])],"derivedFrom":subQ1}),1.0]])]});}
            var Q12;
            {var subQ0=sQuery(id+"F4.wireOp",EDGE,"E14");var subQ1=sQuery(id+"F4.wireOp",EDGE,"E7");var subQ2=makeQuery(id+"F4.imprint","INTERSECT",VERTEX,{"disambiguationData":[OD(0.0)],"derivedFrom":[subQ1,subQ0]});Q12=makeQuery(id+"F4.imprint","IMPRINT",FACE,{"disambiguationData":[TD([[makeQuery(id+"F4.imprint","IMPRINT",EDGE,{"disambiguationData":[TD([[subQ2,-1.0]])],"derivedFrom":subQ1}),1.0]])]});}
            var Q13;
            {var subQ0=sQuery(id+"F4.wireOp",EDGE,"E12");var subQ1=sQuery(id+"F4.wireOp",EDGE,"E2");var subQ2=makeQuery(id+"F4.imprint","INTERSECT",VERTEX,{"disambiguationData":[OD(0.0)],"derivedFrom":[subQ1,subQ0]});Q13=makeQuery(id+"F4.imprint","IMPRINT",FACE,{"disambiguationData":[TD([[makeQuery(id+"F4.imprint","IMPRINT",EDGE,{"disambiguationData":[TD([[subQ2,1.0]])],"derivedFrom":subQ1}),1.0]])]});}
            var Q14;
            {var subQ0=sQuery(id+"F4.wireOp",EDGE,"E14");var subQ1=sQuery(id+"F4.wireOp",EDGE,"E2");var subQ2=makeQuery(id+"F4.imprint","INTERSECT",VERTEX,{"derivedFrom":[subQ1,subQ0]});Q14=makeQuery(id+"F4.imprint","IMPRINT",FACE,{"disambiguationData":[TD([[makeQuery(id+"F4.imprint","IMPRINT",EDGE,{"disambiguationData":[TD([[subQ2,-1.0]])],"derivedFrom":subQ1}),1.0]])]});}
            var Q15;
            {var subQ0=sQuery(id+"F4.wireOp",EDGE,"E14");var subQ1=sQuery(id+"F4.wireOp",EDGE,"E2");var subQ2=makeQuery(id+"F4.imprint","INTERSECT",VERTEX,{"derivedFrom":[subQ1,subQ0]});Q15=makeQuery(id+"F4.imprint","IMPRINT",FACE,{"disambiguationData":[TD([[makeQuery(id+"F4.imprint","IMPRINT",EDGE,{"disambiguationData":[TD([[subQ2,1.0]])],"derivedFrom":subQ1}),1.0]])]});}
            extrude(context, id + "F14", {"entities" : qUnion([Q0, Q1, Q2, Q3, Q4, Q5, Q6, Q7, Q8, Q9, Q10, Q11, Q12, Q13, Q14, Q15]), "operationType" : NewBodyOperationType.REMOVE, "oppositeDirection" : true, "depth" : (getVariable(context, 'Extrude')) * mm});
        }
        {
            var Q0;
            Q0=makeQuery(id+"F2.opExtrude","CAP_EDGE",EDGE,{"disambiguationData":[OSD([sQuery(id+"F1.wireOp",EDGE,"E0.left")])],"isStart":false});
            var Q1;
            Q1=makeQuery(id+"F2.opExtrude","SWEPT_EDGE",EDGE,{"disambiguationData":[OSD([sQuery(id+"F1.wireOp",EDGE,"E0.top"),sQuery(id+"F1.wireOp",EDGE,"E0.left")])]});
            var Q2;
            Q2=makeQuery(id+"F2.opExtrude","SWEPT_EDGE",EDGE,{"disambiguationData":[OSD([sQuery(id+"F1.wireOp",EDGE,"E0.bottom"),sQuery(id+"F1.wireOp",EDGE,"E0.left")])]});
            var Q3;
            Q3=makeQuery(id+"F2.opExtrude","CAP_EDGE",EDGE,{"disambiguationData":[OSD([sQuery(id+"F1.wireOp",EDGE,"E0.left")])],"isStart":true});
            var Q4;
            Q4=makeQuery(id+"F2.opExtrude","SWEPT_EDGE",EDGE,{"disambiguationData":[OSD([sQuery(id+"F1.wireOp",EDGE,"E0.top"),sQuery(id+"F1.wireOp",EDGE,"E0.right")])]});
            var Q5;
            Q5=makeQuery(id+"F2.opExtrude","SWEPT_EDGE",EDGE,{"disambiguationData":[OSD([sQuery(id+"F1.wireOp",EDGE,"E0.bottom"),sQuery(id+"F1.wireOp",EDGE,"E0.right")])]});
            var Q6;
            Q6=makeQuery(id+"F2.opExtrude","CAP_EDGE",EDGE,{"disambiguationData":[OSD([sQuery(id+"F1.wireOp",EDGE,"E0.top")])],"isStart":false});
            var Q7;
            Q7=makeQuery(id+"F2.opExtrude","CAP_EDGE",EDGE,{"disambiguationData":[OSD([sQuery(id+"F1.wireOp",EDGE,"E0.bottom")])],"isStart":false});
            var Q8;
            Q8=makeQuery(id+"F2.opExtrude","CAP_EDGE",EDGE,{"disambiguationData":[OSD([sQuery(id+"F1.wireOp",EDGE,"E0.right")])],"isStart":false});
            var Q9;
            Q9=makeQuery(id+"F2.opExtrude","CAP_EDGE",EDGE,{"disambiguationData":[OSD([sQuery(id+"F1.wireOp",EDGE,"E0.bottom")])],"isStart":true});
            var Q10;
            Q10=makeQuery(id+"F2.opExtrude","CAP_EDGE",EDGE,{"disambiguationData":[OSD([sQuery(id+"F1.wireOp",EDGE,"E0.right")])],"isStart":true});
            var Q11;
            Q11=makeQuery(id+"F2.opExtrude","CAP_EDGE",EDGE,{"disambiguationData":[OSD([sQuery(id+"F1.wireOp",EDGE,"E0.top")])],"isStart":true});
            fillet(context, id + "F15", {"entities" : qUnion([Q0, Q1, Q2, Q3, Q4, Q5, Q6, Q7, Q8, Q9, Q10, Q11]), "radius" : 1.5 * mm, "tangentPropagation" : true, "allowEdgeOverflow" : false});
        }
    });
